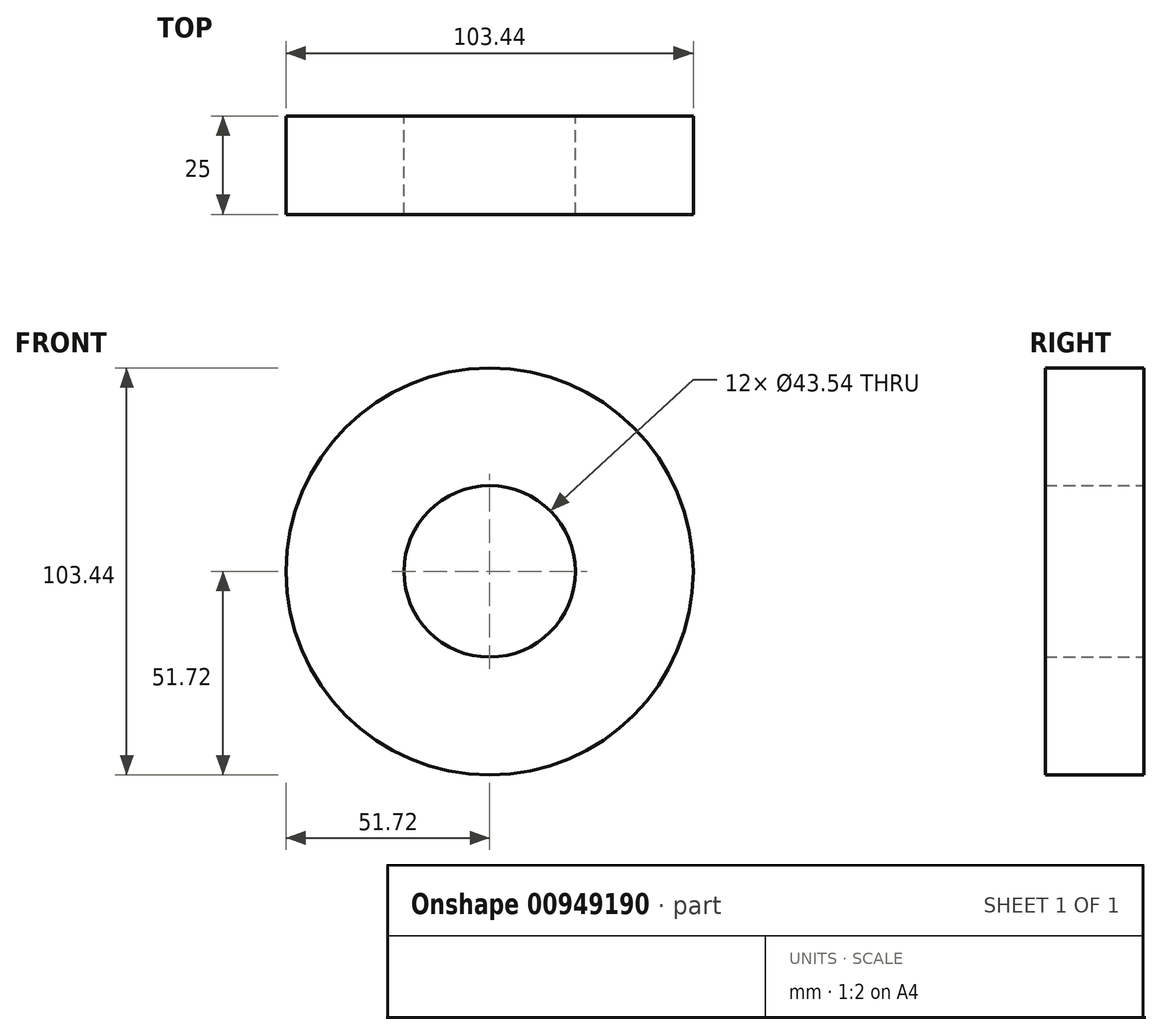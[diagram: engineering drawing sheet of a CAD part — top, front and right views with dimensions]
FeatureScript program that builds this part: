
annotation { "Feature Type Name" : "Feature", "Feature Type Description" : "" }
export const myFeature = defineFeature(function(context is Context, id is Id, definition is map)
    precondition{}
    {
        {
            var Q0;
            Q0=qCreatedBy(makeId("Front.planeOp"),FACE);
            var sketch = newSketch(context, id + "F0", { "sketchPlane" : qUnion([Q0])});
            skCircle(sketch, "E0", {"center": v(0, 0) * mm, "radius": 51.72 * mm});
            skCircle(sketch, "E1", {"center": v(0, 0) * mm, "radius": 21.77 * mm});
            skSolve(sketch);
        }
        {
            var Q0;
            Q0=makeQuery(id+"F0.imprint","IMPRINT",FACE,{"disambiguationData":[TD([[makeQuery(id+"F0.imprint","IMPRINT",EDGE,{"derivedFrom":sQuery(id+"F0.wireOp",EDGE,"E0")}),1.0]])]});
            extrude(context, id + "F1", {"entities" : qUnion([Q0]), "depth" : 25 * mm, "offsetDistance" : 25 * mm});
        }
    });
